# Revit family: Shower_Bar-GROHE-New_Tempesta_Cosmopolitan-27522000
name_source: partatom
category: Specialty Equipment
revit_build: Autodesk Revit 2014 (Build: 20130308_1515(x64)
units: mm (PartAtom-declared; Revit-internal decimal feet)

## types (1)
- 27522000
    Assembly Code = D2010710
    CalGreen Compliant = Yes
    Default Elevation = 68"
    Description = New Tempesta Cosmopolitan 36" Shower Bar
    Finish = Metal-Grohe-000-Chrome
    Height = 36 7/32"
    Installation Type = Wall Mounted
    Length = 3 3/16"
    Manufacturer = Grohe
    Material = Metal-Grohe-000-Chrome
    Model = 27522000
    Price = Prices may vary. Please consult Manufacturer Representative for most up-to-date price list.
    Product Page URL = https://www.grohe.us
    URL = https://www.grohe.us
    Warranty Documentation Link = https://cdn.cloud.grohe.com
    Width = 2 7/8"
    cUPC Compliant = Yes

## geometry (parser evidence)
native form markers: Sweep x3
no freeform markers — native parametric forms only
